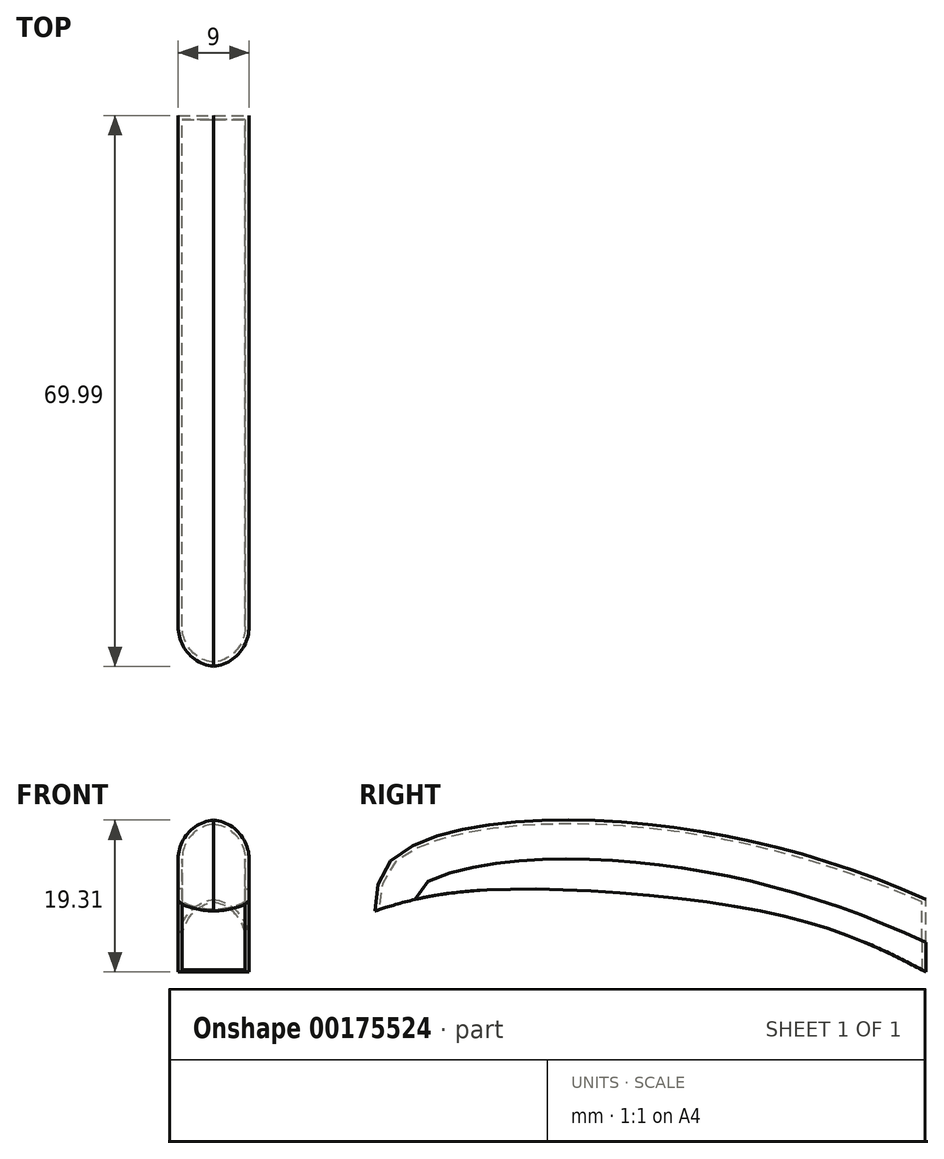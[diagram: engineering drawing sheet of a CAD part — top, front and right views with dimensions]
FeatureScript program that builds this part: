
annotation { "Feature Type Name" : "Feature", "Feature Type Description" : "" }
export const myFeature = defineFeature(function(context is Context, id is Id, definition is map)
    precondition{}
    {
        {
            var Q0;
            Q0=qCreatedBy(makeId("Right.planeOp"),FACE);
            var sketch = newSketch(context, id + "F0", { "sketchPlane" : qUnion([Q0])});
            skFitSpline(sketch, "E0", {"points": [v(-59.06, 10.23) * mm, v(-46.27, 12.8) * mm, v(-7.11, 9.58) * mm, v(10.96, 2.48) * mm], "startDerivative": vector(40.06, 12.89) * mm, "endDerivative": vector(48.08, -25.33) * mm});
            skFitSpline(sketch, "E1", {"points": [v(-59.06, 10.23) * mm, v(-55.68, 17.76) * mm, v(10.96, 11.71) * mm], "startDerivative": vector(1.66, 36.68) * mm, "endDerivative": vector(117.58, -53.13) * mm});
            skLineSegment(sketch, "E2", {"start": v(10.96, 11.71) * mm, "end": v(10.96, 2.48) * mm});
            skLineSegment(sketch, "E3", {"start": v(10.96, 0) * mm, "end": v(-59.04, 0) * mm, "construction": true});
            skLineSegment(sketch, "E4", {"start": v(-59.04, 0) * mm, "end": v(-58.91, 33.42) * mm, "construction": true});
            skSolve(sketch);
        }
        {
            var Q0;
            Q0=qSketchRegion(id+"F0",true);
            extrude(context, id + "F1", {"entities" : qUnion([Q0]), "depth" : 9 * mm});
        }
        {
            var Q0;
            Q0=makeQuery(id+"F1.opExtrude","CAP_EDGE",EDGE,{"disambiguationData":[OSD([sQuery(id+"F0.wireOp",EDGE,"E1")])],"isStart":true});
            var Q1;
            Q1=makeQuery(id+"F1.opExtrude","CAP_EDGE",EDGE,{"disambiguationData":[OSD([sQuery(id+"F0.wireOp",EDGE,"E1")])],"isStart":false});
            fillet(context, id + "F2", {"entities" : qUnion([Q0, Q1]), "radius" : 5 * mm, "tangentPropagation" : true, "allowEdgeOverflow" : false});
        }
        {
            var Q0;
            Q0=makeQuery(id+"F1.opExtrude","SWEPT_FACE",FACE,{"disambiguationData":[OSD([sQuery(id+"F0.wireOp",EDGE,"E0")])]});
            shell(context, id + "F3", {"entities" : qUnion([Q0]), "thickness" : 0.5 * mm});
        }
    });
